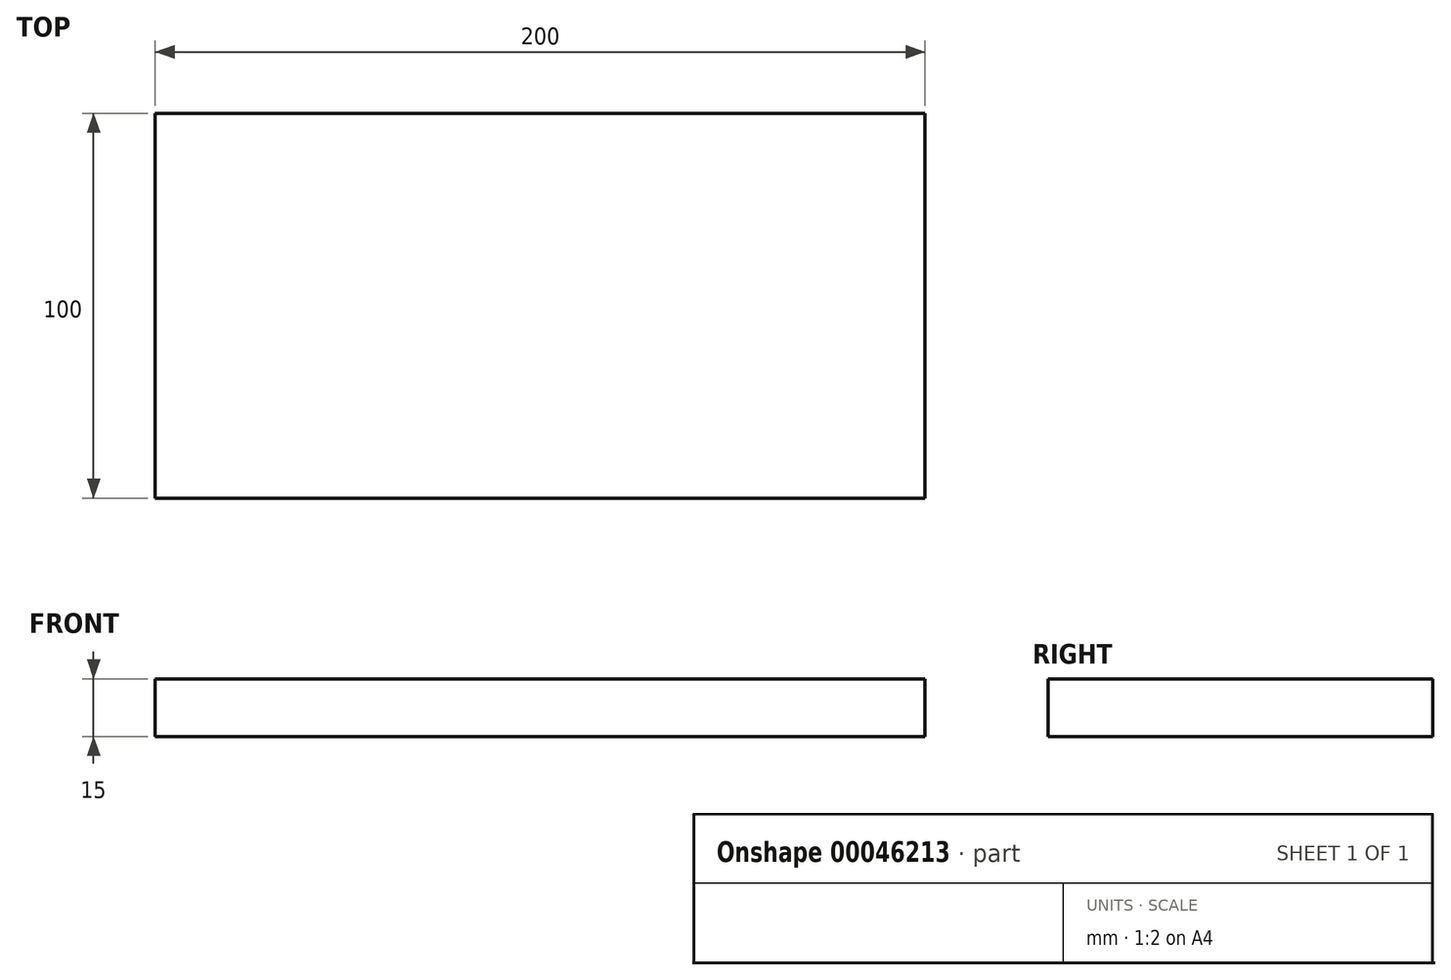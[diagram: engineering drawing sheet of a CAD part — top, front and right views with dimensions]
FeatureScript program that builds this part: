
annotation { "Feature Type Name" : "Feature", "Feature Type Description" : "" }
export const myFeature = defineFeature(function(context is Context, id is Id, definition is map)
    precondition{}
    {
        {
            var Q0;
            Q0=qCreatedBy(makeId("Top.planeOp"),FACE);
            var sketch = newSketch(context, id + "F0", { "sketchPlane" : qUnion([Q0])});
            skLineSegment(sketch, "E0.bottom", {"start": v(0, 0) * mm, "end": v(200, 0) * mm});
            skLineSegment(sketch, "E0.top", {"start": v(0, 100) * mm, "end": v(200, 100) * mm});
            skLineSegment(sketch, "E0.left", {"start": v(0, 0) * mm, "end": v(0, 100) * mm});
            skLineSegment(sketch, "E0.right", {"start": v(200, 0) * mm, "end": v(200, 100) * mm});
            skSolve(sketch);
        }
        {
            var Q0;
            Q0=makeQuery(id+"F0.imprint","IMPRINT",FACE,{"disambiguationData":[TD([[makeQuery(id+"F0.imprint","IMPRINT",EDGE,{"derivedFrom":sQuery(id+"F0.wireOp",EDGE,"E0.bottom")}),1.0]])]});
            extrude(context, id + "F1", {"entities" : qUnion([Q0]), "depth" : 15 * mm});
        }
    });
